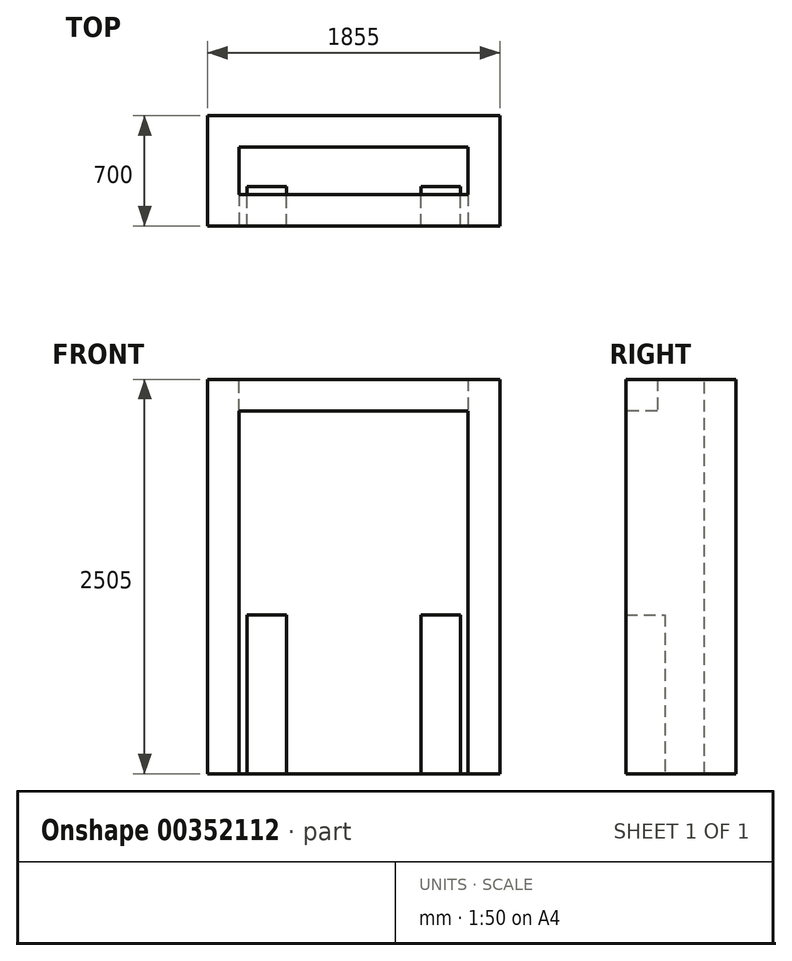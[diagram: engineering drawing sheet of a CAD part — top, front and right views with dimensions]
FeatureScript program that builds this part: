
annotation { "Feature Type Name" : "Feature", "Feature Type Description" : "" }
export const myFeature = defineFeature(function(context is Context, id is Id, definition is map)
    precondition{}
    {
        {
            var Q0;
            Q0=qCreatedBy(makeId("Top.planeOp"),FACE);
            var sketch = newSketch(context, id + "F0", { "sketchPlane" : qUnion([Q0])});
            skLineSegment(sketch, "E0.top", {"start": v(-927.5, -500) * mm, "end": v(927.5, -500) * mm});
            skLineSegment(sketch, "E0.left", {"start": v(-927.5, 200) * mm, "end": v(-927.5, -500) * mm});
            skLineSegment(sketch, "E0.right", {"start": v(927.5, 200) * mm, "end": v(927.5, -500) * mm});
            skLineSegment(sketch, "E1", {"start": v(0, 200) * mm, "end": v(0, -500) * mm, "construction": true});
            skLineSegment(sketch, "E2", {"start": v(-927.5, 200) * mm, "end": v(927.5, 200) * mm});
            skSolve(sketch);
        }
        {
            var Q0;
            Q0 = qSketchRegion(id + "F0", true);
            extrude(context, id + "F1", {"entities" : qUnion([Q0]), "depth" : (2305 + 200) * mm});
        }
        {
            var Q0;
            Q0=makeQuery(id+"F1.opExtrude","SWEPT_FACE",FACE,{"disambiguationData":[OSD([sQuery(id+"F0.wireOp",EDGE,"E0.top")])]});
            var sketch = newSketch(context, id + "F2", { "sketchPlane" : qUnion([Q0])});
            skLineSegment(sketch, "E3.bottom", {"start": v(-727.5, 0) * mm, "end": v(727.5, 0) * mm});
            skLineSegment(sketch, "E3.top", {"start": v(-727.5, 2305) * mm, "end": v(727.5, 2305) * mm});
            skLineSegment(sketch, "E3.left", {"start": v(-727.5, 0) * mm, "end": v(-727.5, 2305) * mm});
            skLineSegment(sketch, "E3.right", {"start": v(727.5, 0) * mm, "end": v(727.5, 2305) * mm});
            skLineSegment(sketch, "E4", {"start": v(0, 2305) * mm, "end": v(0, 0) * mm, "construction": true});
            skLineSegment(sketch, "E5", {"start": v(0, 2505) * mm, "end": v(0, 0) * mm, "construction": true});
            skSolve(sketch);
        }
        {
            var Q0;
            Q0 = qSketchRegion(id + "F2", true);
            extrude(context, id + "F3", {"entities" : qUnion([Q0]), "operationType" : NewBodyOperationType.REMOVE, "oppositeDirection" : true, "depth" : 500 * mm});
        }
        {
            var Q0;
            Q0=makeQuery(id+"F3.boolean.opBoolean","COPY",FACE,{"derivedFrom":makeQuery(id+"F3.opExtrude","SWEPT_FACE",FACE,{"disambiguationData":[OSD([sQuery(id+"F2.wireOp",EDGE,"E3.top")])]})});
            var sketch = newSketch(context, id + "F4", { "sketchPlane" : qUnion([Q0])});
            skLineSegment(sketch, "E6.bottom", {"start": v(-727.5, 0) * mm, "end": v(727.5, 0) * mm});
            skLineSegment(sketch, "E6.top", {"start": v(-727.5, 300) * mm, "end": v(727.5, 300) * mm});
            skLineSegment(sketch, "E6.left", {"start": v(-727.5, 0) * mm, "end": v(-727.5, 300) * mm});
            skLineSegment(sketch, "E6.right", {"start": v(727.5, 0) * mm, "end": v(727.5, 300) * mm});
            skSolve(sketch);
        }
        {
            var Q0;
            Q0 = qSketchRegion(id + "F4", true);
            extrude(context, id + "F5", {"entities" : qUnion([Q0]), "operationType" : NewBodyOperationType.REMOVE, "endBound" : BoundingType.THROUGH_ALL, "oppositeDirection" : true, "depth" : 25 * mm});
        }
        {
            var Q0;
            Q0=qCreatedBy(makeId("Top.planeOp"),FACE);
            var sketch = newSketch(context, id + "F6", { "sketchPlane" : qUnion([Q0])});
            skLineSegment(sketch, "E7.bottom", {"start": v(-677.5, -500) * mm, "end": v(-427.5, -500) * mm});
            skLineSegment(sketch, "E7.top", {"start": v(-677.5, -250) * mm, "end": v(-427.5, -250) * mm});
            skLineSegment(sketch, "E7.left", {"start": v(-677.5, -500) * mm, "end": v(-677.5, -250) * mm});
            skLineSegment(sketch, "E7.right", {"start": v(-427.5, -500) * mm, "end": v(-427.5, -250) * mm});
            skSolve(sketch);
        }
        {
            var Q0;
            Q0 = qSketchRegion(id + "F6", true);
            extrude(context, id + "F7", {"entities" : qUnion([Q0]), "depth" : 1010 * mm});
        }
        {
            var Q0;
            Q0=makeQuery(id+"F7.opExtrude","SWEPT_BODY",BODY,{"disambiguationData":[OSD([sQuery(id+"F6.wireOp",EDGE,"E7.bottom"),sQuery(id+"F6.wireOp",EDGE,"E7.top"),sQuery(id+"F6.wireOp",EDGE,"E7.left"),sQuery(id+"F6.wireOp",EDGE,"E7.right")])]});
            var Q1;
            Q1=qCreatedBy(makeId("Right.planeOp"),FACE);
            mirror(context, id + "F8", {"entities" : qUnion([Q0]), "mirrorPlane" : qUnion([Q1])});
        }
    });
